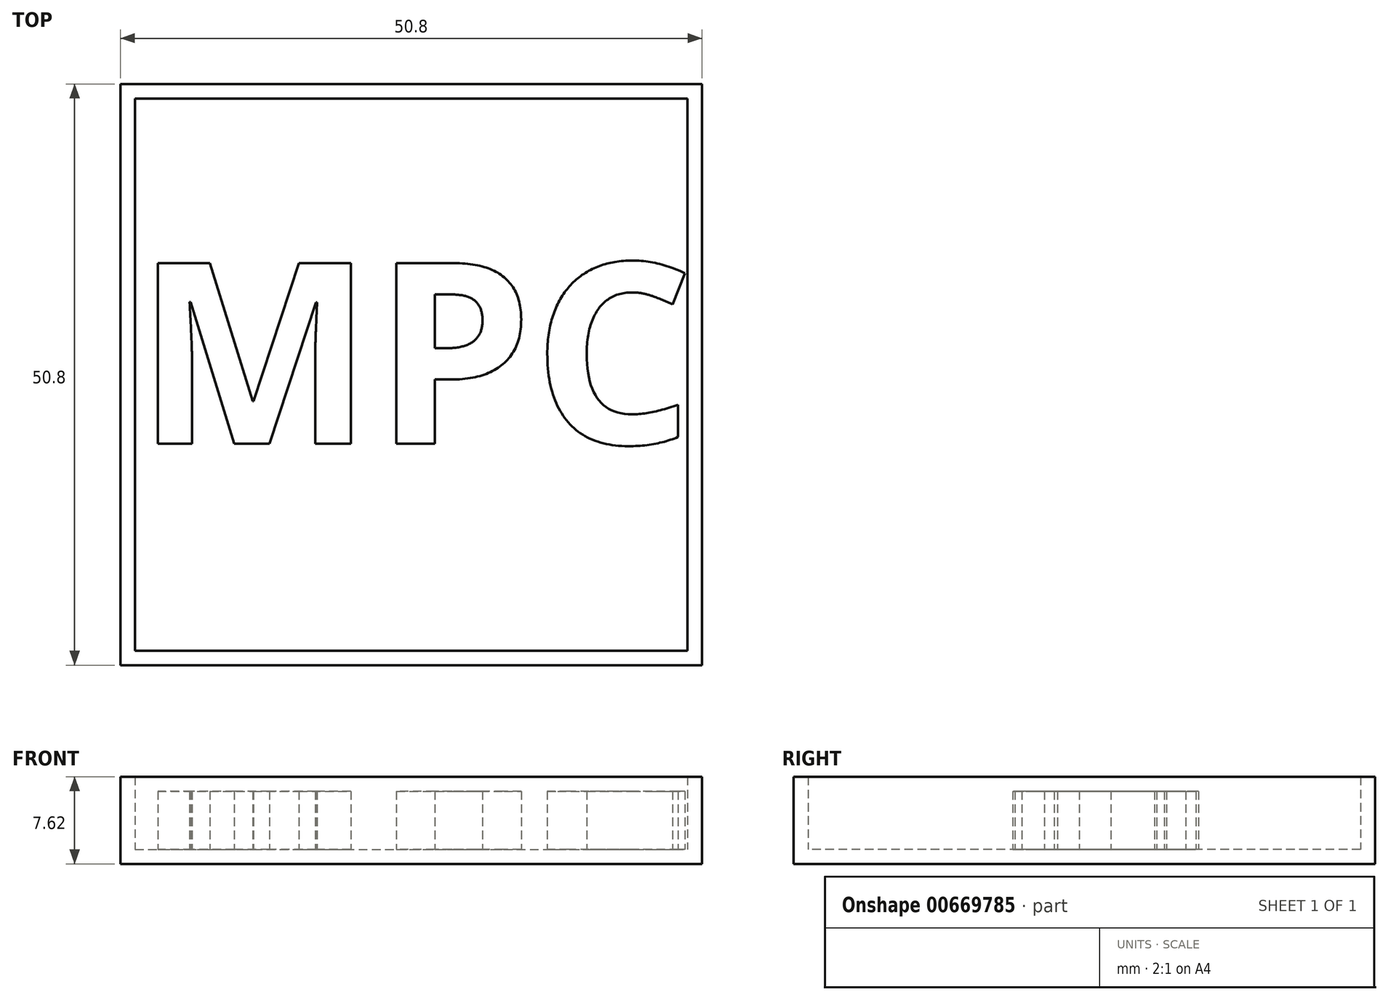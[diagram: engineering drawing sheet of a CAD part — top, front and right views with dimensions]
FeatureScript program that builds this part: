
annotation { "Feature Type Name" : "Feature", "Feature Type Description" : "" }
export const myFeature = defineFeature(function(context is Context, id is Id, definition is map)
    precondition{}
    {
        {
            var Q0;
            Q0=qCreatedBy(makeId("Top.planeOp"),FACE);
            var sketch = newSketch(context, id + "F0", { "sketchPlane" : qUnion([Q0])});
            skLineSegment(sketch, "E0.bottom", {"start": v(-31.4, 41.93) * mm, "end": v(19.4, 41.93) * mm});
            skLineSegment(sketch, "E0.top", {"start": v(-31.4, -8.87) * mm, "end": v(19.4, -8.87) * mm});
            skLineSegment(sketch, "E0.left", {"start": v(-31.4, 41.93) * mm, "end": v(-31.4, -8.87) * mm});
            skLineSegment(sketch, "E0.right", {"start": v(19.4, 41.93) * mm, "end": v(19.4, -8.87) * mm});
            skSolve(sketch);
        }
        {
            var Q0;
            Q0 = qSketchRegion(id + "F0", true);
            extrude(context, id + "F1", {"entities" : qUnion([Q0]), "depth" : 7.62 * mm, "offsetDistance" : 25.4 * mm});
        }
        {
            var Q0;
            Q0=makeQuery(id+"F1.opExtrude","CAP_FACE",FACE,{"disambiguationData":[OSD([sQuery(id+"F0.wireOp",EDGE,"E0.bottom"),sQuery(id+"F0.wireOp",EDGE,"E0.top"),sQuery(id+"F0.wireOp",EDGE,"E0.left"),sQuery(id+"F0.wireOp",EDGE,"E0.right")])],"isStart":false});
            shell(context, id + "F2", {"entities" : qUnion([Q0]), "thickness" : 1.27 * mm});
        }
        {
            var Q0;
            Q0=makeQuery(id+"F2.opShell","OFFSET_FACE",FACE,{"disambiguationData":[OSD([sQuery(id+"F0.wireOp",EDGE,"E0.bottom"),sQuery(id+"F0.wireOp",EDGE,"E0.top"),sQuery(id+"F0.wireOp",EDGE,"E0.left"),sQuery(id+"F0.wireOp",EDGE,"E0.right")])]});
            var sketch = newSketch(context, id + "F3", { "sketchPlane" : qUnion([Q0])});
            skText(sketch, "E1", { "text": "MPC", "fontName": "OpenSans-Bold.ttf"});
            const initialGuessF3  = {"E1": [-0.03013, 0.01048, 1, 0, 0.01592]};
            skSetInitialGuess(sketch, initialGuessF3);
            skSolve(sketch);
        }
        {
            var Q0;
            Q0 = qSketchRegion(id + "F3", true);
            extrude(context, id + "F4", {"entities" : qUnion([Q0]), "operationType" : NewBodyOperationType.ADD, "depth" : 5.08 * mm, "offsetDistance" : 25.4 * mm});
        }
    });
